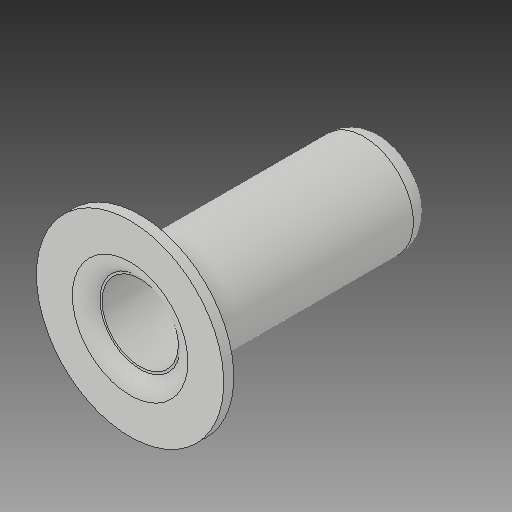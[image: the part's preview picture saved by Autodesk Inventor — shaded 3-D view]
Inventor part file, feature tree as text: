
AUTODESK INVENTOR PART (.ipt)
format: ipt  version: 2018 (Build 220112000, 112)  size: 128,000 bytes
history: native  units: in
note: dims shown in document units (in); Inventor stores cm internally (conversion verified against a paired STEP export)
features: fillet x1
ambient origin geometry x8: Origin, YZ Plane, XZ Plane, XY Plane, X Axis, Y Axis, Z Axis, Center Point
bodies: Solid1 (feature_tree)
feature tree (1):
  fillet  "Fillet1"  [1 undecoded]
note: 1 required parameter value undecoded (feature->parameter linkage not recoverable at this tier; creation-order binding heuristic only, values carry confidence <= 0.55)
